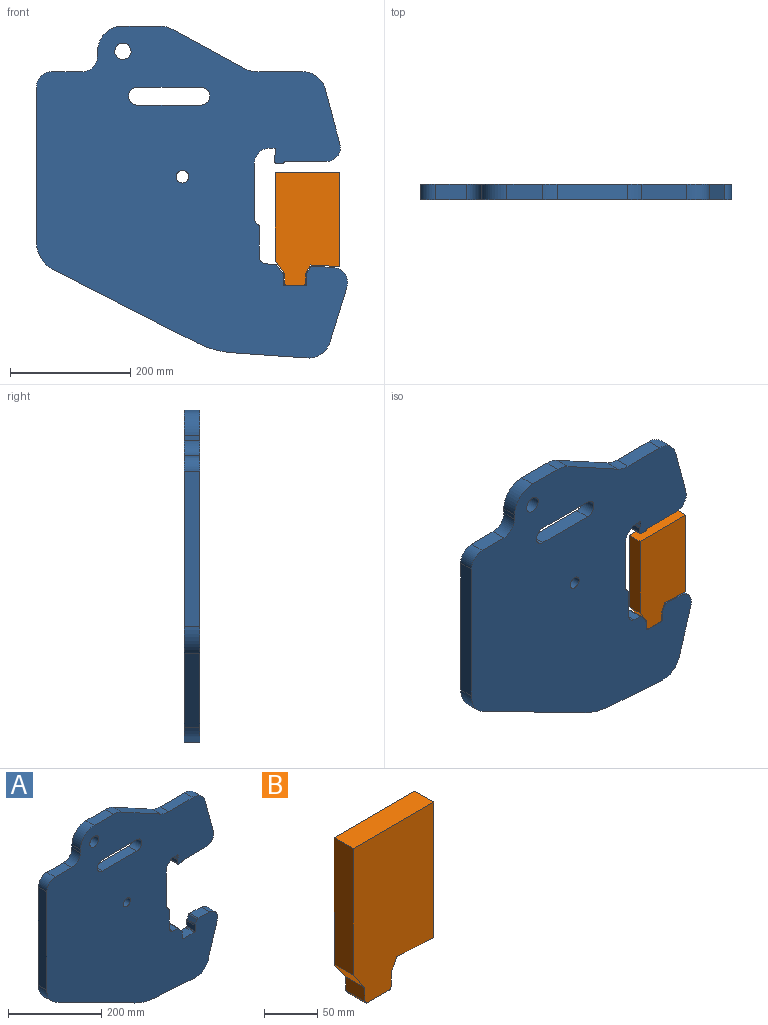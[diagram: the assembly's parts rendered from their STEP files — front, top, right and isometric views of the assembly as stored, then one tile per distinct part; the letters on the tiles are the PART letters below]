
ASSEMBLY  parts=2 mates=1
PART A: 59 faces, bbox 517.5x25.4x552.5 mm
  f0: cylinder r=14.99mm len=29.97mm, axis (0,-1,0), area 1195.8mm2, adj f1,f55,f57,f58
  f1: plane 104.78x25.4mm, normal (0,0,-1), area 2661.3mm2, adj f0,f2,f57,f58
  f2: cylinder r=14.99mm len=29.97mm, axis (0,-1,0), area 1195.8mm2, adj f1,f55,f57,f58
  f3: plane 74.81x25.4mm, normal (0,0,1), area 1900.2mm2, adj f4,f54,f57,f58
  f4: cylinder r=38.1mm len=36.8mm, axis (0,-1,0), area 1266.8mm2, adj f3,f5,f57,f58
  f5: plane 92.02x25.4mm, normal (0.97,0,0.26), area 2419.8mm2, adj f4,f6,f57,f58
  f6: cylinder r=23.01mm len=28.96mm, axis (0,-1,0), area 1071mm2, adj f5,f7,f57,f58
  f7: plane 69.11x25.4mm, normal (0,0,-1), area 1755.5mm2, adj f6,f8,f57,f58
  f8: cylinder r=6.35mm len=25.4mm, axis (0,-1,0), area 168.9mm2, adj f7,f9,f57,f58
  f9: plane 25.4x8.96mm, normal (0,0,-1), area 227.5mm2, adj f8,f10,f57,f58
  f10: cylinder r=3.17mm len=25.4mm, axis (0,-1,0), area 126.7mm2, adj f9,f11,f57,f58
  f11: plane 25.4x8.78mm, normal (-1,0,0), area 222.9mm2, adj f10,f12,f57,f58
  f12: cylinder r=3.17mm len=25.4mm, axis (0,-1,0), area 37.4mm2, adj f11,f13,f57,f58
  f13: plane 25.4x3.74mm, normal (-0.89,0,0.45), area 106.2mm2, adj f12,f14,f57,f58
  f14: cylinder r=3.17mm len=25.4mm, axis (0,-1,0), area 37.4mm2, adj f13,f15,f57,f58
  f15: plane 25.4x3.7mm, normal (-1,0,0), area 93.9mm2, adj f14,f16,f57,f58
  f16: cylinder r=3.17mm len=25.4mm, axis (0,-1,0), area 126.7mm2, adj f15,f17,f57,f58
  f17: plane 25.4x7.24mm, normal (0,0,-1), area 183.9mm2, adj f16,f18,f57,f58
  f18: cylinder r=25.4mm len=25.4mm, axis (0,-1,0), area 1013.4mm2, adj f17,f19,f57,f58
  f19: plane 90.41x25.4mm, normal (1,0,0), area 2296.4mm2, adj f18,f20,f57,f58
  f20: cylinder r=14.18mm len=25.4mm, axis (0,-1,0), area 357.6mm2, adj f19,f21,f57,f58
  f21: cylinder r=3.17mm len=25.4mm, axis (0,-1,0), area 80.1mm2, adj f20,f22,f57,f58
  f22: plane 49.61x25.4mm, normal (1,0,0), area 1260.2mm2, adj f21,f23,f57,f58
  f23: cylinder r=12.7mm len=25.4mm, axis (0,-1,0), area 489.8mm2, adj f22,f24,f57,f58
  f24: plane 25.4x15.03mm, normal (0.06,0,1), area 382.5mm2, adj f23,f25,f57,f58
  f25: cylinder r=3.17mm len=25.4mm, axis (0,-1,0), area 71.7mm2, adj f24,f26,f57,f58
  f26: plane 25.4x13.75mm, normal (0.81,0,0.59), area 432.2mm2, adj f25,f27,f57,f58
  f27: cylinder r=6.35mm len=25.4mm, axis (0,-1,0), area 101.6mm2, adj f26,f28,f57,f58
  f28: plane 25.4x13.67mm, normal (1,0,0), area 347.3mm2, adj f27,f29,f57,f58
  f29: cylinder r=2.54mm len=25.4mm, axis (0,-1,0), area 101.3mm2, adj f28,f30,f57,f58
  f30: plane 33.02x25.4mm, normal (0,0,1), area 838.7mm2, adj f29,f31,f57,f58
  f31: cylinder r=2.54mm len=25.4mm, axis (0,-1,0), area 101.3mm2, adj f30,f32,f57,f58
  f32: plane 25.4x14.6mm, normal (-1,0,0), area 370.9mm2, adj f31,f33,f57,f58
  f33: cylinder r=6.35mm len=25.4mm, axis (0,-1,0), area 76mm2, adj f32,f34,f57,f58
  f34: plane 25.4x10.24mm, normal (-0.89,0,0.45), area 291.9mm2, adj f33,f35,f57,f58
  f35: cylinder r=3.17mm len=25.4mm, axis (0,-1,0), area 92.9mm2, adj f34,f36,f57,f58
  f36: plane 35.29x25.4mm, normal (0.05,0,1), area 897.5mm2, adj f35,f37,f57,f58
  f37: cylinder r=25.4mm len=32.79mm, axis (0,-1,0), area 1171.1mm2, adj f36,f38,f57,f58
  f38: plane 91.04x27.83mm, normal (0.96,0,-0.29), area 2418.1mm2, adj f37,f39,f57,f58
  f39: cylinder r=38.1mm len=39.09mm, axis (0,-1,0), area 1300.5mm2, adj f38,f40,f57,f58
  f40: plane 123.75x25.4mm, normal (-0.07,0,-1), area 3151mm2, adj f39,f41,f57,f58
  f41: cylinder r=152.4mm len=58.56mm, axis (0,-1,0), area 1553.9mm2, adj f40,f42,f57,f58
  f42: plane 239.44x122mm, normal (-0.45,0,-0.89), area 6825.7mm2, adj f41,f43,f57,f58
  f43: cylinder r=50.8mm len=45.26mm, axis (0,-1,0), area 1418.8mm2, adj f42,f44,f57,f58
  f44: plane 258.6x25.4mm, normal (-1,0,0), area 6568.5mm2, adj f43,f45,f57,f58
  f45: cylinder r=25.4mm len=25.4mm, axis (0,-1,0), area 1013.4mm2, adj f44,f46,f57,f58
  f46: plane 50.8x25.4mm, normal (0,0,1), area 1290.3mm2, adj f45,f47,f57,f58
  f47: cylinder r=25.4mm len=25.4mm, axis (0,-1,0), area 1013.4mm2, adj f46,f48,f57,f58
  f48: plane 25.4x8.64mm, normal (-1,0,0), area 219.4mm2, adj f47,f49,f57,f58
  f49: cylinder r=42.16mm len=42.16mm, axis (0,-1,0), area 1682.3mm2, adj f48,f50,f57,f58
  f50: plane 59.18x25.4mm, normal (0,0,1), area 1503.2mm2, adj f49,f51,f57,f58
  f51: cylinder r=50.8mm len=25.4mm, axis (0,-1,0), area 644.3mm2, adj f50,f52,f57,f58
  f52: plane 116.96x63.79mm, normal (0.48,0,0.88), area 3383.9mm2, adj f51,f54,f57,f58
  f53: cylinder r=13.59mm len=27.18mm, axis (0,-1,0), area 2168.7mm2, adj f57,f58
  f54: cylinder r=50.8mm len=25.4mm, axis (0,-1,0), area 644.3mm2, adj f3,f52,f57,f58
  f55: plane 104.78x25.4mm, normal (0,0,1), area 2661.3mm2, adj f0,f2,f57,f58
  f56: cylinder r=10.54mm len=25.4mm, axis (0,-1,0), area 1682.3mm2, adj f57,f58
  f57: plane 552.45x517.53mm, normal (0,1,0), area 193976.6mm2, adj f0,f1,f2,f3,f4,f5,f6,f7
  f58: plane 552.45x517.53mm, normal (0,-1,0), area 193976.6mm2, adj f0,f1,f2,f3,f4,f5,f6,f7
PART B: 13 faces, bbox 108x25.4x187.3 mm
  f0: plane 25.4x15.84mm, normal (-1,0,0), area 402.4mm2, adj f1,f10,f11,f12
  f1: plane 25.4x22.26mm, normal (-0.81,0,-0.58), area 694.4mm2, adj f0,f2,f11,f12
  f2: plane 146.05x25.4mm, normal (-1,0,0), area 3709.7mm2, adj f1,f3,f11,f12
  f3: plane 107.95x25.4mm, normal (0,0,1), area 2741.9mm2, adj f2,f4,f11,f12
  f4: plane 156.54x25.4mm, normal (1,0,0), area 3976.1mm2, adj f3,f5,f11,f12
  f5: plane 49.46x25.4mm, normal (-0.05,0,-1), area 1258.1mm2, adj f4,f6,f11,f12
  f6: plane 25.4x14.81mm, normal (0.89,0,-0.46), area 423.9mm2, adj f5,f7,f11,f12
  f7: plane 25.4x15.47mm, normal (1,0,0), area 392.9mm2, adj f6,f8,f11,f12
  f8: cylinder r=3.17mm len=25.4mm, axis (0,-1,0), area 126.7mm2, adj f7,f9,f11,f12
  f9: plane 28.58x25.4mm, normal (0,0,-1), area 725.8mm2, adj f8,f10,f11,f12
  f10: cylinder r=3.17mm len=25.4mm, axis (0,-1,0), area 126.7mm2, adj f0,f9,f11,f12
  f11: plane 187.33x107.95mm, normal (0,1,0), area 17950mm2, adj f0,f1,f2,f3,f4,f5,f6,f7
  f12: plane 187.33x107.95mm, normal (0,-1,0), area 17950mm2, adj f0,f1,f2,f3,f4,f5,f6,f7
PLACE A t=(0.76,11,-39.95)mm fixed
PLACE B t=(153.17,11,-156.72)mm
MATE planar A.f43 <-> B.f12  axis (0,-1,0) through (-208.76,-14.4,-85.82)mm
